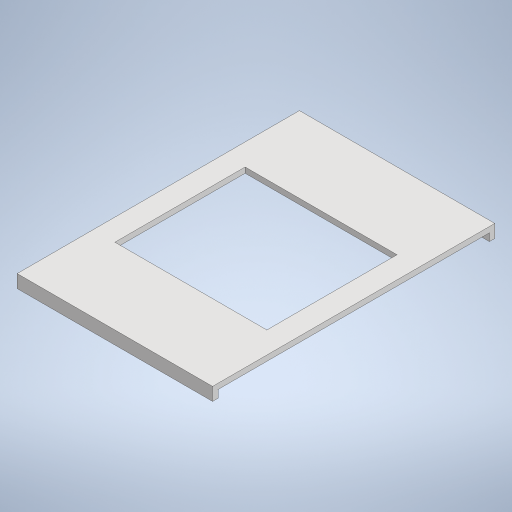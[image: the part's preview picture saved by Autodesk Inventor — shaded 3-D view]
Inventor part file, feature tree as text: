
AUTODESK INVENTOR PART (.ipt)
format: ipt  version: 2024 (Build 280153000, 153)  size: 244,736 bytes
history: native  units: mm
features: extrude x3, sketch x3
ambient origin geometry x8: Origin, YZ Plane, XZ Plane, XY Plane, X Axis, Y Axis, Z Axis, Center Point
bodies: Solid1 (feature_tree)
feature tree (6):
  extrude  "Extrusion1"  Depth=180.0mm
  extrude  "Extrusion2"  Depth=5.0mm
  extrude  "Extrusion3"  Depth=7.0mm TaperAngle=0.0deg
  sketch  "Sketch1"  dims[d0=260.0mm d1=180.0mm]
  sketch  "Sketch2"  dims[d2=5.0mm d3=0.0mm d4=5.0mm]
  sketch  "Sketch3"  dims[d5=5.0mm d6=7.0mm d7=0.0mm d8=20.0mm d9=20.0mm d10=70.0mm d11=70.0mm d12=0.0mm d13=0.0mm]
